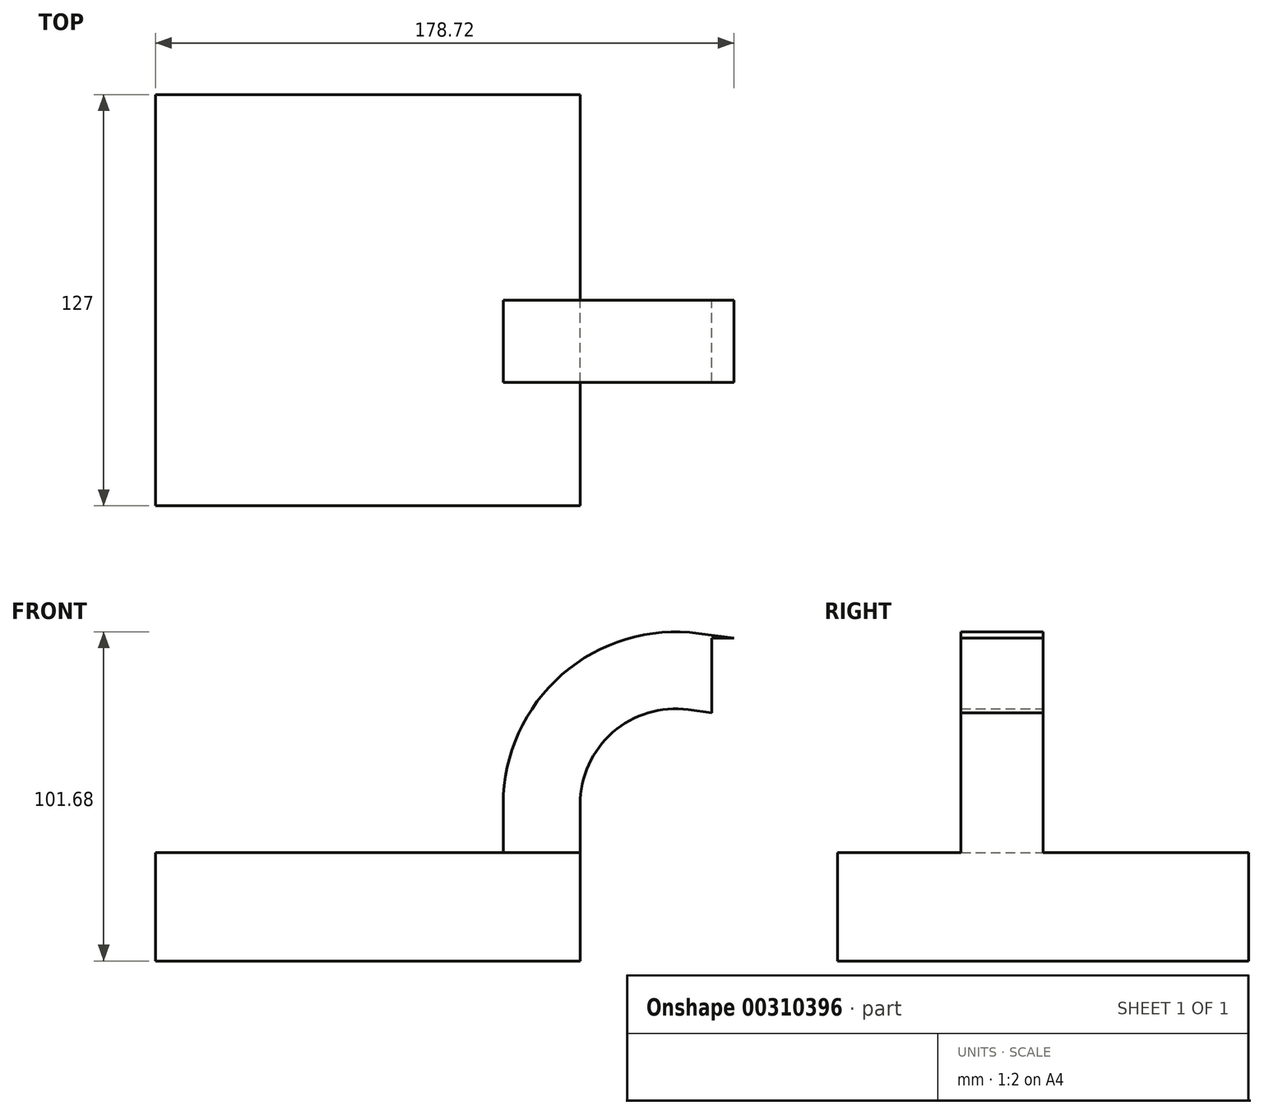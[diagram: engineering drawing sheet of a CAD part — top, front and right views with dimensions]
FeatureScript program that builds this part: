
annotation { "Feature Type Name" : "Feature", "Feature Type Description" : "" }
export const myFeature = defineFeature(function(context is Context, id is Id, definition is map)
    precondition{}
    {
        {
            var Q0;
            Q0=qCreatedBy(makeId("Front.planeOp"),FACE);
            var sketch = newSketch(context, id + "F0", { "sketchPlane" : qUnion([Q0])});
            skLineSegment(sketch, "E0.bottom", {"start": v(65.6, 16.73) * mm, "end": v(-65.6, 16.73) * mm});
            skLineSegment(sketch, "E0.top", {"start": v(65.6, -16.73) * mm, "end": v(-65.6, -16.73) * mm});
            skLineSegment(sketch, "E0.left", {"start": v(65.6, 16.73) * mm, "end": v(65.6, -16.73) * mm});
            skLineSegment(sketch, "E0.right", {"start": v(-65.6, 16.73) * mm, "end": v(-65.6, -16.73) * mm});
            skPoint(sketch, "E0.middle", {"position": v(0, 0) * mm});
            skLineSegment(sketch, "E1.bottom", {"start": v(187.37, 49.36) * mm, "end": v(106.26, 49.36) * mm});
            skLineSegment(sketch, "E1.top", {"start": v(187.37, 83) * mm, "end": v(106.26, 83) * mm});
            skLineSegment(sketch, "E1.left", {"start": v(187.37, 49.36) * mm, "end": v(187.37, 83) * mm});
            skLineSegment(sketch, "E1.right", {"start": v(106.26, 49.36) * mm, "end": v(106.26, 83) * mm});
            skPoint(sketch, "E1.middle", {"position": v(146.81, 66.18) * mm});
            skLineSegment(sketch, "E2", {"start": v(65.6, 16.73) * mm, "end": v(65.6, 31.73) * mm});
            skArc(sketch, "E3", {"start": v(65.6, 31.73) * mm, "mid": v(75.68, 53.92) * mm, "end": v(99.02, 60.93) * mm});
            skLineSegment(sketch, "E4", {"start": v(99.02, 60.93) * mm, "end": v(135.37, 56) * mm});
            skLineSegment(sketch, "E5.0", {"start": v(71.95, 16.73) * mm, "end": v(71.95, 31.73) * mm});
            skLineSegment(sketch, "E6.0", {"start": v(102.21, 84.47) * mm, "end": v(138.55, 79.55) * mm});
            skArc(sketch, "E6.1", {"start": v(41.85, 31.73) * mm, "mid": v(60.05, 71.8) * mm, "end": v(102.21, 84.47) * mm});
            skLineSegment(sketch, "E6.2", {"start": v(41.85, 16.73) * mm, "end": v(41.85, 31.73) * mm});
            skSolve(sketch);
        }
        {
            var Q0;
            Q0=makeQuery(id+"F0.imprint","IMPRINT",FACE,{"disambiguationData":[TD([[makeQuery(id+"F0.imprint","IMPRINT",EDGE,{"derivedFrom":sQuery(id+"F0.wireOp",EDGE,"E0.top")}),-1.0]])]});
            extrude(context, id + "F1", {"entities" : qUnion([Q0]), "endBound" : BoundingType.SYMMETRIC, "depth" : 127 * mm});
        }
        {
            var Q0;
            {var subQ0=sQuery(id+"F0.wireOp",EDGE,"E2");Q0=makeQuery(id+"F0.imprint","IMPRINT",FACE,{"disambiguationData":[TD([[makeQuery(id+"F0.imprint","IMPRINT",EDGE,{"derivedFrom":subQ0}),1.0]])]});}
            extrude(context, id + "F2", {"entities" : qUnion([Q0]), "operationType" : NewBodyOperationType.ADD, "depth" : 25.4 * mm});
        }
    });
